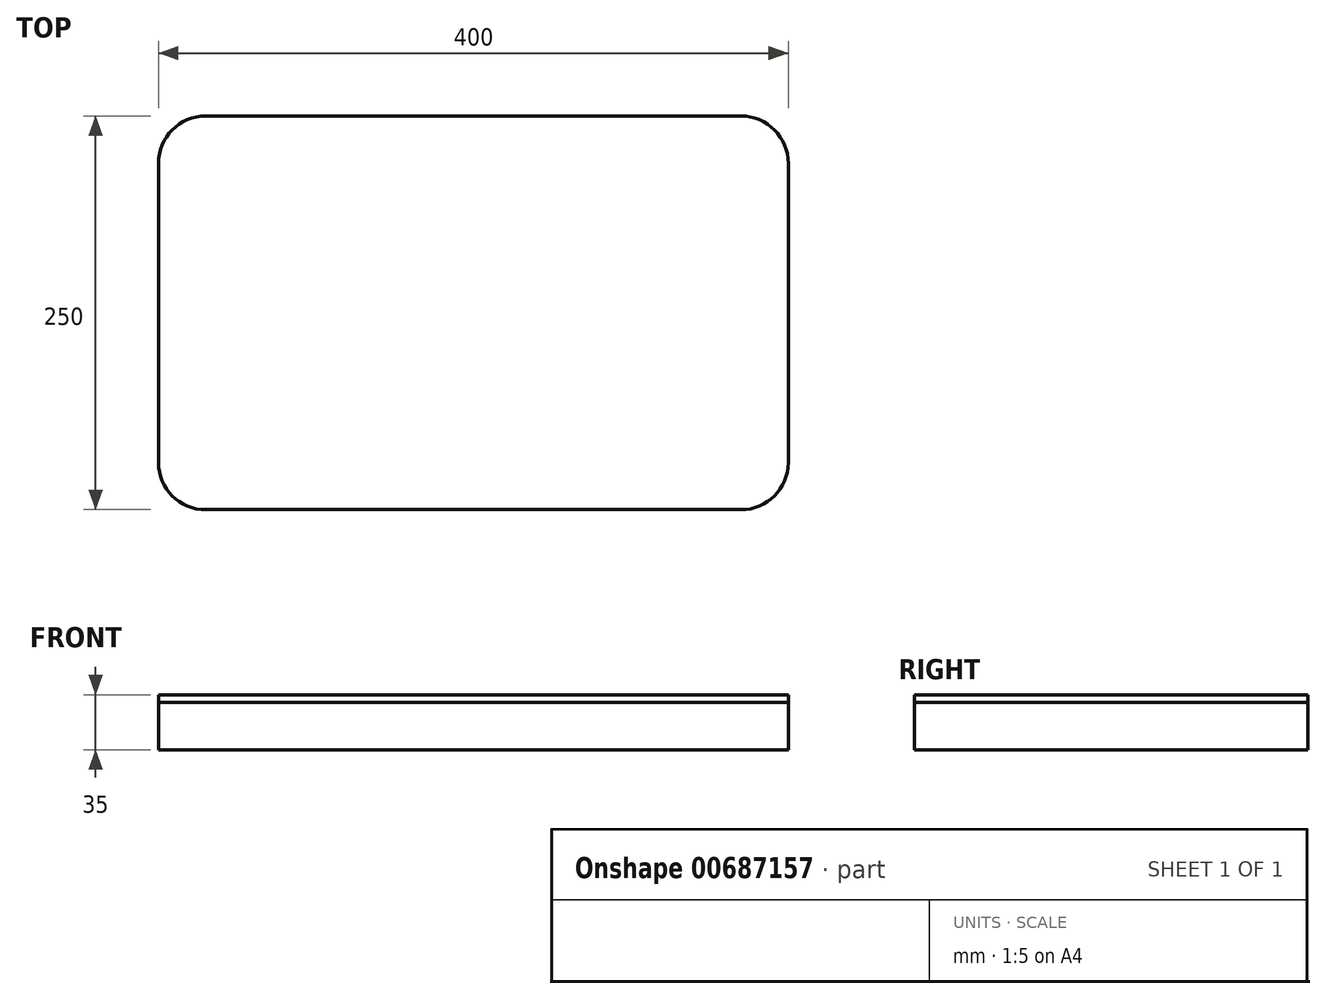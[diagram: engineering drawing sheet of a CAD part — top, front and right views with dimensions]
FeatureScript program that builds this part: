
annotation { "Feature Type Name" : "Feature", "Feature Type Description" : "" }
export const myFeature = defineFeature(function(context is Context, id is Id, definition is map)
    precondition{}
    {
        {
            var Q0;
            Q0=qCreatedBy(makeId("Top.planeOp"),FACE);
            var sketch = newSketch(context, id + "F0", { "sketchPlane" : qUnion([Q0])});
            skLineSegment(sketch, "E0.bottom", {"start": v(200, -125) * mm, "end": v(-200, -125) * mm});
            skLineSegment(sketch, "E0.top", {"start": v(200, 125) * mm, "end": v(-200, 125) * mm});
            skLineSegment(sketch, "E0.left", {"start": v(200, -125) * mm, "end": v(200, 125) * mm});
            skLineSegment(sketch, "E0.right", {"start": v(-200, -125) * mm, "end": v(-200, 125) * mm});
            skPoint(sketch, "E0.middle", {"position": v(0, 0) * mm});
            skSolve(sketch);
        }
        {
            var Q0;
            Q0=makeQuery(id+"F0.imprint","IMPRINT",FACE,{"disambiguationData":[TD([[makeQuery(id+"F0.imprint","IMPRINT",EDGE,{"derivedFrom":sQuery(id+"F0.wireOp",EDGE,"E0.bottom")}),-1.0]])]});
            extrude(context, id + "F1", {"entities" : qUnion([Q0]), "depth" : 30 * mm, "offsetDistance" : 25 * mm});
        }
        {
            var Q0;
            Q0=makeQuery(id+"F1.opExtrude","SWEPT_EDGE",EDGE,{"disambiguationData":[OSD([sQuery(id+"F0.wireOp",EDGE,"E0.bottom"),sQuery(id+"F0.wireOp",EDGE,"E0.right")])]});
            var Q1;
            Q1=makeQuery(id+"F1.opExtrude","SWEPT_EDGE",EDGE,{"disambiguationData":[OSD([sQuery(id+"F0.wireOp",EDGE,"E0.bottom"),sQuery(id+"F0.wireOp",EDGE,"E0.left")])]});
            var Q2;
            Q2=makeQuery(id+"F1.opExtrude","SWEPT_EDGE",EDGE,{"disambiguationData":[OSD([sQuery(id+"F0.wireOp",EDGE,"E0.top"),sQuery(id+"F0.wireOp",EDGE,"E0.left")])]});
            var Q3;
            Q3=makeQuery(id+"F1.opExtrude","SWEPT_EDGE",EDGE,{"disambiguationData":[OSD([sQuery(id+"F0.wireOp",EDGE,"E0.top"),sQuery(id+"F0.wireOp",EDGE,"E0.right")])]});
            fillet(context, id + "F2", {"entities" : qUnion([Q0, Q1, Q2, Q3]), "radius" : 30 * mm, "tangentPropagation" : true, "allowEdgeOverflow" : false});
        }
        {
            var Q0;
            Q0=makeQuery(id+"F1.opExtrude","CAP_FACE",FACE,{"disambiguationData":[OSD([sQuery(id+"F0.wireOp",EDGE,"E0.bottom"),sQuery(id+"F0.wireOp",EDGE,"E0.top"),sQuery(id+"F0.wireOp",EDGE,"E0.left"),sQuery(id+"F0.wireOp",EDGE,"E0.right")])],"isStart":false});
            extrude(context, id + "F3", {"entities" : qUnion([Q0]), "depth" : 5 * mm, "offsetDistance" : 25 * mm});
        }
    });
